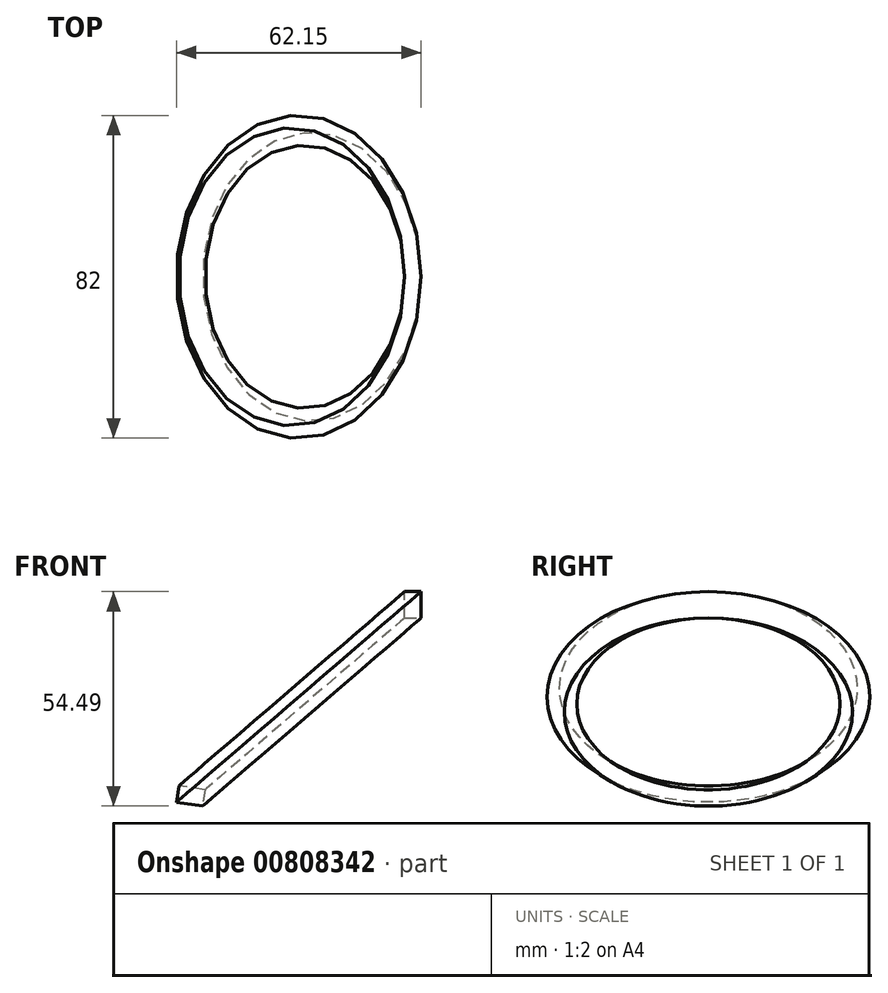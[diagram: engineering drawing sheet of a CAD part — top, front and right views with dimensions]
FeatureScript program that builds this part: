
annotation { "Feature Type Name" : "Feature", "Feature Type Description" : "" }
export const myFeature = defineFeature(function(context is Context, id is Id, definition is map)
    precondition{}
    {
        {
            var Q0;
            Q0=qCreatedBy(makeId("Front.planeOp"),FACE);
            var sketch = newSketch(context, id + "F0", { "sketchPlane" : qUnion([Q0])});
            skLineSegment(sketch, "E0.bottom", {"start": v(-42.94, 36.5) * mm, "end": v(39.3, 36.5) * mm});
            skLineSegment(sketch, "E0.top", {"start": v(-42.94, 12.45) * mm, "end": v(39.3, 12.45) * mm});
            skLineSegment(sketch, "E0.left", {"start": v(-42.94, 36.5) * mm, "end": v(-42.94, 12.45) * mm});
            skLineSegment(sketch, "E0.right", {"start": v(39.3, 36.5) * mm, "end": v(39.3, 12.45) * mm});
            skLineSegment(sketch, "E1.bottom", {"start": v(27.84, 43.22) * mm, "end": v(23.64, 43.22) * mm});
            skLineSegment(sketch, "E1.top", {"start": v(27.84, 15.8) * mm, "end": v(23.64, 15.8) * mm});
            skLineSegment(sketch, "E1.left", {"start": v(27.84, 43.22) * mm, "end": v(27.84, 15.8) * mm});
            skLineSegment(sketch, "E1.right", {"start": v(23.64, 43.22) * mm, "end": v(23.64, 15.8) * mm});
            skLineSegment(sketch, "E2", {"start": v(-30.35, 47.98) * mm, "end": v(-11.33, 25.88) * mm});
            skSolve(sketch);
        }
        {
            var Q0;
            {var subQ5=sQuery(id+"F0.wireOp",EDGE,"E1.bottom");Q0=makeQuery(id+"F0.imprint","IMPRINT",FACE,{"disambiguationData":[TD([[makeQuery(id+"F0.imprint","IMPRINT",EDGE,{"derivedFrom":subQ5}),1.0]])]});}
            var Q1;
            Q1=sQuery(id+"F0.wireOp",EDGE,"E2");
            revolve(context, id + "F1", {"surfaceOperationType" : NewSurfaceOperationType.NEW, "entities" : qUnion([Q0]), "axis" : qUnion([Q1]), "revolveType" : RevolveType.FULL});
        }
    });
